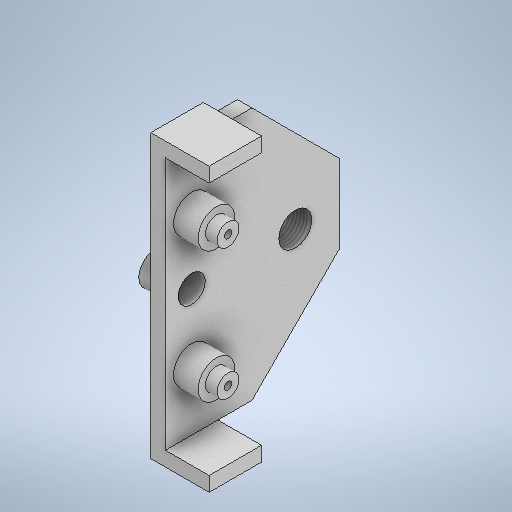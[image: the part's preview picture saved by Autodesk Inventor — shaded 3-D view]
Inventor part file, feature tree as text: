
AUTODESK INVENTOR PART (.ipt)
format: ipt  version: 2025.2 (Build 292293000, 293)  size: 401,408 bytes
history: native  units: in
note: dims shown in document units (in); Inventor stores cm internally (conversion verified against a paired STEP export)
features: extrude x6, other x5, plane x1, hole x1, sketch x1
ambient origin geometry x8: Origin, YZ Plane, XZ Plane, XY Plane, X Axis, Y Axis, Z Axis, Center Point
bodies: Volumenkörper1 (feature_tree)
feature tree (14):
  other  "Skelett_Laufkatze.ipt"
  extrude  "Grundplatte"  Depth=0.3937in TaperAngle=0.0deg
  extrude  "Wellenöffnung_für_Kettenzug"  Depth=0.3937in TaperAngle=0.0deg
  extrude  "Laufradaufhängung_1"  Depth=0.3937in TaperAngle=0.0deg
  extrude  "Laufradaufhängung_2"  Depth=0.3937in TaperAngle=0.0deg
  extrude  "Schutzwände"  Depth=0.3937in TaperAngle=0.0deg
  extrude  "Schraubbolzenöffnung"  Depth=0.3937in TaperAngle=0.0deg
  other  "Schraubbolzengewinde"
  plane  "Arbeitsebene1"
  hole  "Bohrung1"  [1 undecoded]
  other  "Fuehrungsplatte_seite_Kettenzug"
  other  "Fuehrungsplatte_Laufradaufhängung_Kettenzug"
  other  "Fuehrungsplatte_Schraubbolzen_Kettenzug"
  sketch  "Skizze4"  dims[d0=0.3937in d1=0.3937in d2=0.0in d3=0.3937in d4=0.0in d5=0.3937in d6=0.0in d7=0.3937in d8=0.0in d9=0.3937in d10=0.0in d11=0.3937in d12=0.0in d13=1.9685in d14=0.0in d15=0.0in d16=0.3979in d17=0.9449in d18=0.1575in d19=0.0787in d20=90.0deg d21=1.2717in d22=0.8108in]
note: 1 required parameter value undecoded (feature->parameter linkage not recoverable at this tier; creation-order binding heuristic only, values carry confidence <= 0.55)
